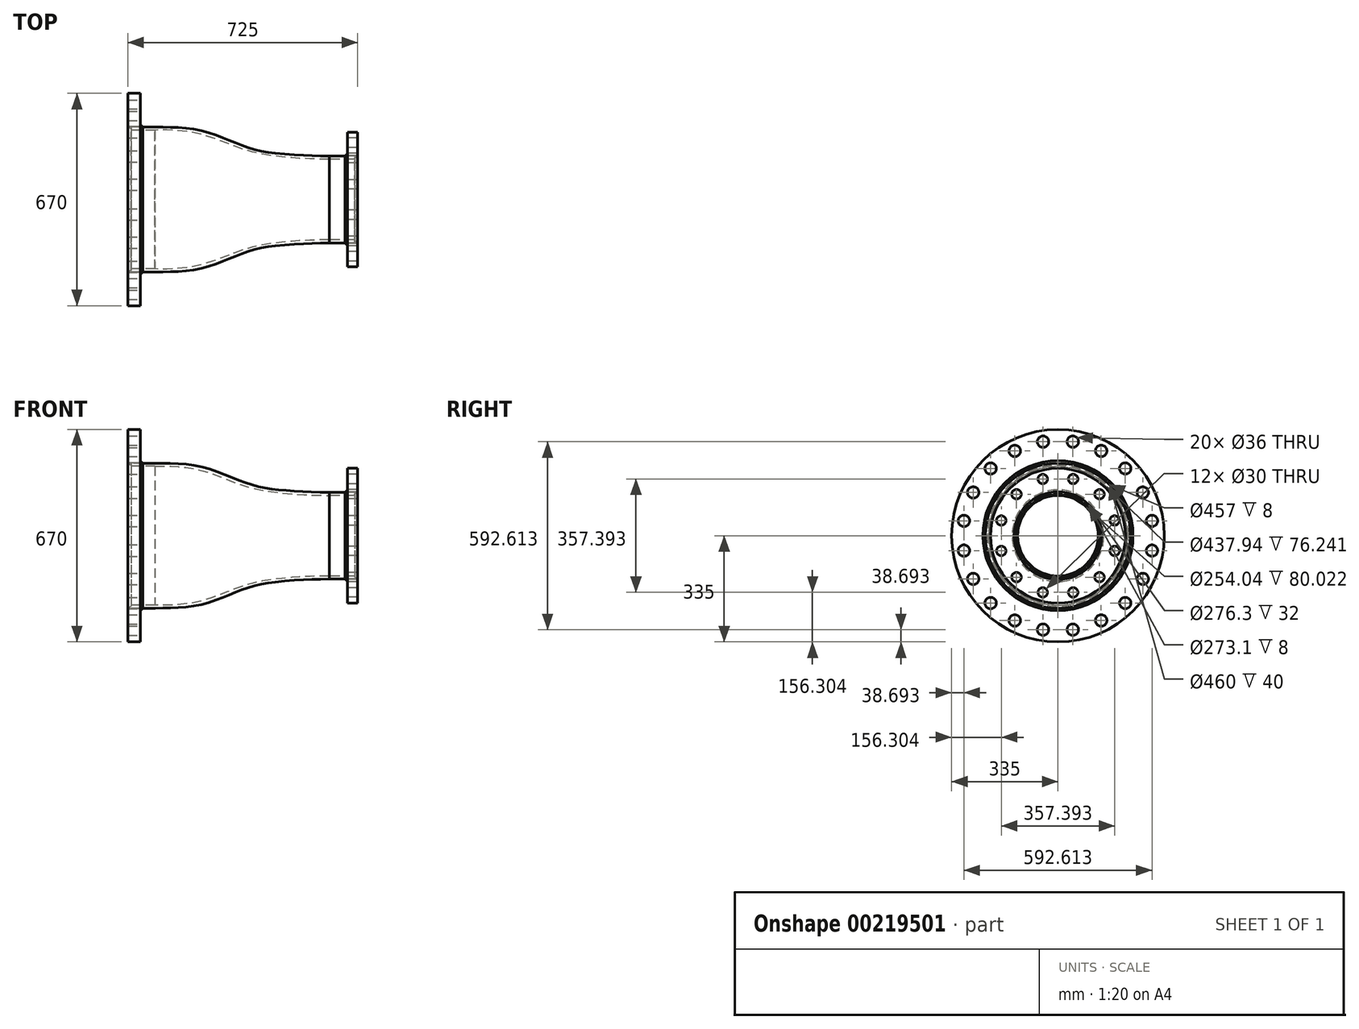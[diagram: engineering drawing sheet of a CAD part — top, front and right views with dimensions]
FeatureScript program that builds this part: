
annotation { "Feature Type Name" : "Feature", "Feature Type Description" : "" }
export const myFeature = defineFeature(function(context is Context, id is Id, definition is map)
    precondition{}
    {
        {
            var Q0;
            Q0=qCreatedBy(makeId("Front.planeOp"),FACE);
            var sketch = newSketch(context, id + "F0", { "sketchPlane" : qUnion([Q0])});
            skLineSegment(sketch, "E0", {"start": v(-562.58, 0) * mm, "end": v(652.64, 0) * mm, "construction": true});
            skLineSegment(sketch, "E1", {"start": v(-329.66, 228.5) * mm, "end": v(-253.37, 228.5) * mm});
            skLineSegment(sketch, "E2", {"start": v(375.34, 136.55) * mm, "end": v(295.32, 136.55) * mm});
            skFitSpline(sketch, "E3", {"points": [v(-253.37, 228.5) * mm, v(-109.72, 217.61) * mm, v(24.3, 169.13) * mm, v(129.85, 145.37) * mm, v(295.32, 136.55) * mm], "startDerivative": vector(539.24, -5.2) * mm, "endDerivative": vector(650.78, -14.67) * mm});
            skLineSegment(sketch, "E4.1", {"start": v(-329.66, 218.97) * mm, "end": v(-253.42, 218.97) * mm});
            skLineSegment(sketch, "E5.0", {"start": v(375.34, 127.02) * mm, "end": v(295.32, 127.02) * mm});
            skLineSegment(sketch, "E6", {"start": v(-329.66, 228.5) * mm, "end": v(-329.66, 218.97) * mm});
            skLineSegment(sketch, "E7", {"start": v(375.34, 136.55) * mm, "end": v(375.34, 127.02) * mm});
            skLineSegment(sketch, "E8.bottom", {"start": v(-299.66, 230) * mm, "end": v(-339.66, 230) * mm});
            skLineSegment(sketch, "E8.top", {"start": v(-299.66, 335) * mm, "end": v(-339.66, 335) * mm});
            skLineSegment(sketch, "E8.left", {"start": v(-299.66, 230) * mm, "end": v(-299.66, 335) * mm});
            skLineSegment(sketch, "E8.right", {"start": v(-339.66, 230) * mm, "end": v(-339.66, 335) * mm});
            skLineSegment(sketch, "E9", {"start": v(-299.66, 230) * mm, "end": v(-299.66, 228.5) * mm});
            skLineSegment(sketch, "E10", {"start": v(-337.66, 230) * mm, "end": v(-329.66, 222) * mm});
            skLineSegment(sketch, "E11", {"start": v(-299.66, 236.5) * mm, "end": v(-291.66, 228.5) * mm});
            skLineSegment(sketch, "E12", {"start": v(-329.66, 230) * mm, "end": v(-329.66, 228.5) * mm});
            skLineSegment(sketch, "E13.bottom", {"start": v(385.34, 138.15) * mm, "end": v(353.34, 138.15) * mm});
            skLineSegment(sketch, "E13.top", {"start": v(385.34, 212.5) * mm, "end": v(353.34, 212.5) * mm});
            skLineSegment(sketch, "E13.left", {"start": v(385.34, 138.15) * mm, "end": v(385.34, 212.5) * mm});
            skLineSegment(sketch, "E13.right", {"start": v(353.34, 138.15) * mm, "end": v(353.34, 212.5) * mm});
            skLineSegment(sketch, "E14", {"start": v(353.34, 138.15) * mm, "end": v(353.34, 136.55) * mm});
            skLineSegment(sketch, "E15", {"start": v(375.34, 138.15) * mm, "end": v(375.34, 136.55) * mm});
            skLineSegment(sketch, "E16", {"start": v(345.34, 136.55) * mm, "end": v(353.34, 144.55) * mm});
            skLineSegment(sketch, "E17", {"start": v(383.34, 138.15) * mm, "end": v(375.34, 130.15) * mm});
            skLineSegment(sketch, "E18", {"start": v(-253.37, 228.5) * mm, "end": v(-253.42, 218.97) * mm});
            skLineSegment(sketch, "E19", {"start": v(295.32, 136.55) * mm, "end": v(295.32, 127.02) * mm});
            skFitSpline(sketch, "E20", {"points": [v(-253.42, 218.97) * mm, v(-209.6, 218.97) * mm, v(-109.6, 206.39) * mm, v(24.68, 158.26) * mm, v(130.86, 136.31) * mm, v(236.57, 128.15) * mm, v(295.32, 127.02) * mm], "startDerivative": vector(341.33, 5.53) * mm, "endDerivative": vector(401.2, -2.2) * mm});
            skSolve(sketch);
        }
        {
            var Q0;
            {var subQ0=sQuery(id+"F0.wireOp",EDGE,"E8.top");Q0=makeQuery(id+"F0.imprint","IMPRINT",FACE,{"disambiguationData":[TD([[makeQuery(id+"F0.imprint","IMPRINT",EDGE,{"derivedFrom":subQ0}),1.0]])]});}
            var Q1;
            Q1=sQuery(id+"F0.wireOp",EDGE,"E0");
            revolve(context, id + "F1", {"entities" : qUnion([Q0]), "axis" : qUnion([Q1]), "revolveType" : RevolveType.FULL});
        }
        {
            var Q0;
            Q0=makeQuery(id+"F0.imprint","IMPRINT",FACE,{"disambiguationData":[TD([[makeQuery(id+"F0.imprint","IMPRINT",EDGE,{"derivedFrom":sQuery(id+"F0.wireOp",EDGE,"E3")}),-1.0]])]});
            var Q1;
            {var subQ0=sQuery(id+"F0.wireOp",EDGE,"E4.1");Q1=makeQuery(id+"F0.imprint","IMPRINT",FACE,{"disambiguationData":[TD([[makeQuery(id+"F0.imprint","IMPRINT",EDGE,{"derivedFrom":subQ0}),1.0]])]});}
            var Q2;
            {var subQ0=sQuery(id+"F0.wireOp",EDGE,"E5.0");Q2=makeQuery(id+"F0.imprint","IMPRINT",FACE,{"disambiguationData":[TD([[makeQuery(id+"F0.imprint","IMPRINT",EDGE,{"derivedFrom":subQ0}),-1.0]])]});}
            var Q3;
            Q3=sQuery(id+"F0.wireOp",EDGE,"E0");
            revolve(context, id + "F2", {"entities" : qUnion([Q0, Q1, Q2]), "axis" : qUnion([Q3]), "revolveType" : RevolveType.FULL});
        }
        {
            var Q0;
            {var subQ0=sQuery(id+"F0.wireOp",EDGE,"E13.top");Q0=makeQuery(id+"F0.imprint","IMPRINT",FACE,{"disambiguationData":[TD([[makeQuery(id+"F0.imprint","IMPRINT",EDGE,{"derivedFrom":subQ0}),1.0]])]});}
            var Q1;
            Q1=sQuery(id+"F0.wireOp",EDGE,"E0");
            revolve(context, id + "F3", {"entities" : qUnion([Q0]), "axis" : qUnion([Q1]), "revolveType" : RevolveType.FULL});
        }
        {
            var Q0;
            {var subQ2=sQuery(id+"F0.wireOp",EDGE,"E10");Q0=makeQuery(id+"F0.imprint","IMPRINT",FACE,{"disambiguationData":[TD([[makeQuery(id+"F0.imprint","IMPRINT",EDGE,{"derivedFrom":subQ2}),1.0]])]});}
            var Q1;
            {var subQ0=sQuery(id+"F0.wireOp",EDGE,"E9");Q1=makeQuery(id+"F0.imprint","IMPRINT",FACE,{"disambiguationData":[TD([[makeQuery(id+"F0.imprint","IMPRINT",EDGE,{"derivedFrom":subQ0}),1.0]])]});}
            var Q2;
            {var subQ0=sQuery(id+"F0.wireOp",EDGE,"E14");Q2=makeQuery(id+"F0.imprint","IMPRINT",FACE,{"disambiguationData":[TD([[makeQuery(id+"F0.imprint","IMPRINT",EDGE,{"derivedFrom":subQ0}),-1.0]])]});}
            var Q3;
            {var subQ0=sQuery(id+"F0.wireOp",EDGE,"E15");Q3=makeQuery(id+"F0.imprint","IMPRINT",FACE,{"disambiguationData":[TD([[makeQuery(id+"F0.imprint","IMPRINT",EDGE,{"derivedFrom":subQ0}),1.0]])]});}
            var Q4;
            Q4=sQuery(id+"F0.wireOp",EDGE,"E0");
            revolve(context, id + "F4", {"entities" : qUnion([Q0, Q1, Q2, Q3]), "axis" : qUnion([Q4]), "revolveType" : RevolveType.FULL});
        }
        {
            var Q0;
            Q0=makeQuery(id+"F1.opRevolve","SWEPT_FACE",FACE,{"disambiguationData":[OSD([sQuery(id+"F0.wireOp",EDGE,"E8.right")])]});
            var sketch = newSketch(context, id + "F5", { "sketchPlane" : qUnion([Q0])});
            skCircle(sketch, "E21.cCircle", {"center": v(0, 0) * mm, "radius": 300 * mm, "construction": true});
            skLineSegment(sketch, "E21.0", {"start": v(212.13, 212.13) * mm, "end": v(267.3, 136.2) * mm});
            skLineSegment(sketch, "E21.1", {"start": v(267.3, 136.2) * mm, "end": v(296.3, 46.93) * mm});
            skLineSegment(sketch, "E21.2", {"start": v(296.3, 46.93) * mm, "end": v(296.3, -46.93) * mm});
            skLineSegment(sketch, "E21.3", {"start": v(296.3, -46.93) * mm, "end": v(267.3, -136.2) * mm});
            skLineSegment(sketch, "E21.4", {"start": v(267.3, -136.2) * mm, "end": v(212.13, -212.13) * mm});
            skLineSegment(sketch, "E21.5", {"start": v(212.13, -212.13) * mm, "end": v(136.2, -267.3) * mm});
            skLineSegment(sketch, "E21.6", {"start": v(136.2, -267.3) * mm, "end": v(46.93, -296.3) * mm});
            skLineSegment(sketch, "E21.7", {"start": v(46.93, -296.3) * mm, "end": v(-46.93, -296.3) * mm});
            skLineSegment(sketch, "E21.8", {"start": v(-46.93, -296.3) * mm, "end": v(-136.2, -267.3) * mm});
            skLineSegment(sketch, "E21.9", {"start": v(-136.2, -267.3) * mm, "end": v(-212.13, -212.13) * mm});
            skLineSegment(sketch, "E21.10", {"start": v(-212.13, -212.13) * mm, "end": v(-267.3, -136.2) * mm});
            skLineSegment(sketch, "E21.11", {"start": v(-267.3, -136.2) * mm, "end": v(-296.3, -46.93) * mm});
            skLineSegment(sketch, "E21.12", {"start": v(-296.3, -46.93) * mm, "end": v(-296.3, 46.93) * mm});
            skLineSegment(sketch, "E21.13", {"start": v(-296.3, 46.93) * mm, "end": v(-267.3, 136.2) * mm});
            skLineSegment(sketch, "E21.14", {"start": v(-267.3, 136.2) * mm, "end": v(-212.13, 212.13) * mm});
            skLineSegment(sketch, "E21.15", {"start": v(-212.13, 212.13) * mm, "end": v(-136.2, 267.3) * mm});
            skLineSegment(sketch, "E21.16", {"start": v(-136.2, 267.3) * mm, "end": v(-46.93, 296.3) * mm});
            skLineSegment(sketch, "E21.17", {"start": v(-46.93, 296.3) * mm, "end": v(46.93, 296.3) * mm});
            skLineSegment(sketch, "E21.18", {"start": v(46.93, 296.3) * mm, "end": v(136.2, 267.3) * mm});
            skLineSegment(sketch, "E21.19", {"start": v(136.2, 267.3) * mm, "end": v(212.13, 212.13) * mm});
            skPoint(sketch, "E22", {"position": v(-136.2, 267.3) * mm});
            skPoint(sketch, "E23", {"position": v(-46.93, 296.3) * mm});
            skPoint(sketch, "E24", {"position": v(46.93, 296.3) * mm});
            skPoint(sketch, "E25", {"position": v(136.2, 267.3) * mm});
            skPoint(sketch, "E26", {"position": v(212.13, 212.13) * mm});
            skPoint(sketch, "E27", {"position": v(267.3, 136.2) * mm});
            skPoint(sketch, "E28", {"position": v(296.3, 46.93) * mm});
            skPoint(sketch, "E29", {"position": v(296.3, -46.93) * mm});
            skPoint(sketch, "E30", {"position": v(267.3, -136.2) * mm});
            skPoint(sketch, "E31", {"position": v(212.13, -212.13) * mm});
            skPoint(sketch, "E32", {"position": v(136.2, -267.3) * mm});
            skPoint(sketch, "E33", {"position": v(46.93, -296.3) * mm});
            skPoint(sketch, "E34", {"position": v(-46.93, -296.3) * mm});
            skPoint(sketch, "E35", {"position": v(-136.2, -267.3) * mm});
            skPoint(sketch, "E36", {"position": v(-212.13, -212.13) * mm});
            skPoint(sketch, "E37", {"position": v(-267.3, -136.2) * mm});
            skPoint(sketch, "E38", {"position": v(-296.3, -46.93) * mm});
            skPoint(sketch, "E39", {"position": v(-296.3, 46.93) * mm});
            skPoint(sketch, "E40", {"position": v(-267.3, 136.2) * mm});
            skPoint(sketch, "E41", {"position": v(-212.13, 212.13) * mm});
            skSolve(sketch);
        }
        {
            var Q0;
            Q0=sQuery(id+"F5.wireOp",VERTEX,"E23");
            var Q1;
            Q1=sQuery(id+"F5.wireOp",VERTEX,"E24");
            var Q2;
            Q2=sQuery(id+"F5.wireOp",VERTEX,"E25");
            var Q3;
            Q3=sQuery(id+"F5.wireOp",VERTEX,"E26");
            var Q4;
            Q4=sQuery(id+"F5.wireOp",VERTEX,"E27");
            var Q5;
            Q5=sQuery(id+"F5.wireOp",VERTEX,"E28");
            var Q6;
            Q6=sQuery(id+"F5.wireOp",VERTEX,"E29");
            var Q7;
            Q7=sQuery(id+"F5.wireOp",VERTEX,"E30");
            var Q8;
            Q8=sQuery(id+"F5.wireOp",VERTEX,"E31");
            var Q9;
            Q9=sQuery(id+"F5.wireOp",VERTEX,"E32");
            var Q10;
            Q10=sQuery(id+"F5.wireOp",VERTEX,"E33");
            var Q11;
            Q11=sQuery(id+"F5.wireOp",VERTEX,"E35");
            var Q12;
            Q12=sQuery(id+"F5.wireOp",VERTEX,"E36");
            var Q13;
            Q13=sQuery(id+"F5.wireOp",VERTEX,"E37");
            var Q14;
            Q14=sQuery(id+"F5.wireOp",VERTEX,"E38");
            var Q15;
            Q15=sQuery(id+"F5.wireOp",VERTEX,"E34");
            var Q16;
            Q16=sQuery(id+"F5.wireOp",VERTEX,"E39");
            var Q17;
            Q17=sQuery(id+"F5.wireOp",VERTEX,"E40");
            var Q18;
            Q18=sQuery(id+"F5.wireOp",VERTEX,"E41");
            var Q19;
            Q19=sQuery(id+"F5.wireOp",VERTEX,"E22");
            var Q20;
            Q20=makeQuery(id+"F1.opRevolve","SWEPT_BODY",BODY,{"disambiguationData":[OSD([sQuery(id+"F0.wireOp",EDGE,"E8.bottom"),sQuery(id+"F0.wireOp",EDGE,"E8.top"),sQuery(id+"F0.wireOp",EDGE,"E8.left"),sQuery(id+"F0.wireOp",EDGE,"E8.right")])]});
            hole(context, id + "F6", {"style" : HoleStyle.SIMPLE, "endStyle" : HoleEndStyle.BLIND, "holeDiameter" : 36 * mm, "holeDepth" : 50 * mm, "locations" : qUnion([Q0, Q1, Q2, Q3, Q4, Q5, Q6, Q7, Q8, Q9, Q10, Q11, Q12, Q13, Q14, Q15, Q16, Q17, Q18, Q19]), "scope" : qUnion([Q20])});
        }
        {
            var Q0;
            Q0=makeQuery(id+"F3.opRevolve","SWEPT_FACE",FACE,{"disambiguationData":[OSD([sQuery(id+"F0.wireOp",EDGE,"E13.left")])]});
            var sketch = newSketch(context, id + "F7", { "sketchPlane" : qUnion([Q0])});
            skCircle(sketch, "E42.cCircle", {"center": v(0, 0) * mm, "radius": 185 * mm, "construction": true});
            skLineSegment(sketch, "E42.0", {"start": v(130.81, 130.81) * mm, "end": v(178.7, 47.88) * mm});
            skLineSegment(sketch, "E42.1", {"start": v(178.7, 47.88) * mm, "end": v(178.7, -47.88) * mm});
            skLineSegment(sketch, "E42.2", {"start": v(178.7, -47.88) * mm, "end": v(130.81, -130.81) * mm});
            skLineSegment(sketch, "E42.3", {"start": v(130.81, -130.81) * mm, "end": v(47.88, -178.7) * mm});
            skLineSegment(sketch, "E42.4", {"start": v(47.88, -178.7) * mm, "end": v(-47.88, -178.7) * mm});
            skLineSegment(sketch, "E42.5", {"start": v(-47.88, -178.7) * mm, "end": v(-130.81, -130.81) * mm});
            skLineSegment(sketch, "E42.6", {"start": v(-130.81, -130.81) * mm, "end": v(-178.7, -47.88) * mm});
            skLineSegment(sketch, "E42.7", {"start": v(-178.7, -47.88) * mm, "end": v(-178.7, 47.88) * mm});
            skLineSegment(sketch, "E42.8", {"start": v(-178.7, 47.88) * mm, "end": v(-130.81, 130.81) * mm});
            skLineSegment(sketch, "E42.9", {"start": v(-130.81, 130.81) * mm, "end": v(-47.88, 178.7) * mm});
            skLineSegment(sketch, "E42.10", {"start": v(-47.88, 178.7) * mm, "end": v(47.88, 178.7) * mm});
            skLineSegment(sketch, "E42.11", {"start": v(47.88, 178.7) * mm, "end": v(130.81, 130.81) * mm});
            skPoint(sketch, "E43", {"position": v(130.81, 130.81) * mm});
            skPoint(sketch, "E44", {"position": v(178.7, 47.88) * mm});
            skPoint(sketch, "E45", {"position": v(178.7, -47.88) * mm});
            skPoint(sketch, "E46", {"position": v(130.81, -130.81) * mm});
            skPoint(sketch, "E47", {"position": v(47.88, -178.7) * mm});
            skPoint(sketch, "E48", {"position": v(-47.88, -178.7) * mm});
            skPoint(sketch, "E49", {"position": v(-130.81, -130.81) * mm});
            skPoint(sketch, "E50", {"position": v(-178.7, -47.88) * mm});
            skPoint(sketch, "E51", {"position": v(-178.7, 47.88) * mm});
            skPoint(sketch, "E52", {"position": v(-130.81, 130.81) * mm});
            skPoint(sketch, "E53", {"position": v(-47.88, 178.7) * mm});
            skPoint(sketch, "E54", {"position": v(47.88, 178.7) * mm});
            skSolve(sketch);
        }
        {
            var Q0;
            Q0=sQuery(id+"F7.wireOp",VERTEX,"E44");
            var Q1;
            Q1=sQuery(id+"F7.wireOp",VERTEX,"E45");
            var Q2;
            Q2=sQuery(id+"F7.wireOp",VERTEX,"E46");
            var Q3;
            Q3=sQuery(id+"F7.wireOp",VERTEX,"E47");
            var Q4;
            Q4=sQuery(id+"F7.wireOp",VERTEX,"E48");
            var Q5;
            Q5=sQuery(id+"F7.wireOp",VERTEX,"E49");
            var Q6;
            Q6=sQuery(id+"F7.wireOp",VERTEX,"E50");
            var Q7;
            Q7=sQuery(id+"F7.wireOp",VERTEX,"E51");
            var Q8;
            Q8=sQuery(id+"F7.wireOp",VERTEX,"E52");
            var Q9;
            Q9=sQuery(id+"F7.wireOp",VERTEX,"E53");
            var Q10;
            Q10=sQuery(id+"F7.wireOp",VERTEX,"E54");
            var Q11;
            Q11=sQuery(id+"F7.wireOp",VERTEX,"E43");
            var Q12;
            Q12=makeQuery(id+"F3.opRevolve","SWEPT_BODY",BODY,{"disambiguationData":[OSD([sQuery(id+"F0.wireOp",EDGE,"E13.bottom"),sQuery(id+"F0.wireOp",EDGE,"E13.top"),sQuery(id+"F0.wireOp",EDGE,"E13.left"),sQuery(id+"F0.wireOp",EDGE,"E13.right")])]});
            hole(context, id + "F8", {"style" : HoleStyle.SIMPLE, "endStyle" : HoleEndStyle.BLIND, "holeDiameter" : 30 * mm, "holeDepth" : 50 * mm, "locations" : qUnion([Q0, Q1, Q2, Q3, Q4, Q5, Q6, Q7, Q8, Q9, Q10, Q11]), "scope" : qUnion([Q12])});
        }
    });
